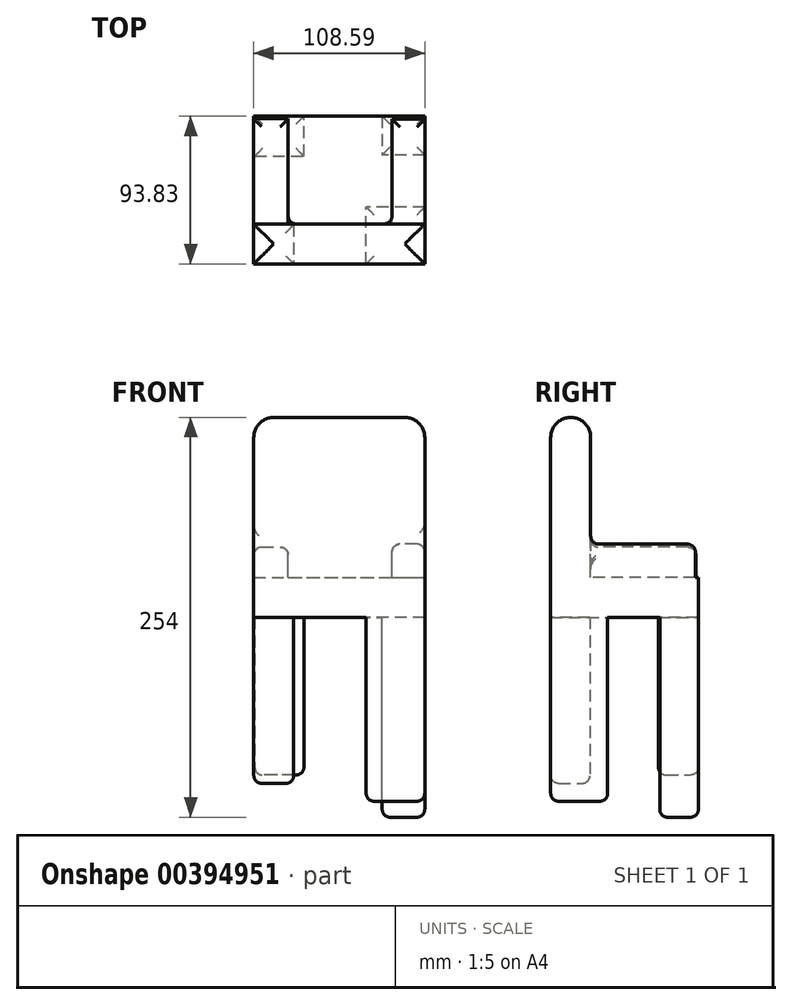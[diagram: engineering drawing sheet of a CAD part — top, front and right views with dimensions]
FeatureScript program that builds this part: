
annotation { "Feature Type Name" : "Feature", "Feature Type Description" : "" }
export const myFeature = defineFeature(function(context is Context, id is Id, definition is map)
    precondition{}
    {
        {
            var Q0;
            Q0=qCreatedBy(makeId("Top.planeOp"),FACE);
            var sketch = newSketch(context, id + "F0", { "sketchPlane" : qUnion([Q0])});
            skLineSegment(sketch, "E0.bottom", {"start": v(-122.47, 127.56) * mm, "end": v(-13.88, 127.56) * mm});
            skLineSegment(sketch, "E0.top", {"start": v(-122.47, 33.73) * mm, "end": v(-13.88, 33.73) * mm});
            skLineSegment(sketch, "E0.left", {"start": v(-122.47, 127.56) * mm, "end": v(-122.47, 33.73) * mm});
            skLineSegment(sketch, "E0.right", {"start": v(-13.88, 127.56) * mm, "end": v(-13.88, 33.73) * mm});
            skSolve(sketch);
        }
        {
            var Q0;
            Q0 = qSketchRegion(id + "F0", true);
            extrude(context, id + "F1", {"entities" : qUnion([Q0]), "depth" : 25.4 * mm});
        }
        {
            var Q0;
            Q0=makeQuery(id+"F1.opExtrude","CAP_FACE",FACE,{"disambiguationData":[OSD([sQuery(id+"F0.wireOp",EDGE,"E0.bottom"),sQuery(id+"F0.wireOp",EDGE,"E0.top"),sQuery(id+"F0.wireOp",EDGE,"E0.left"),sQuery(id+"F0.wireOp",EDGE,"E0.right")])],"isStart":false});
            var sketch = newSketch(context, id + "F2", { "sketchPlane" : qUnion([Q0])});
            skLineSegment(sketch, "E1.bottom", {"start": v(-122.47, 33.73) * mm, "end": v(-13.88, 33.73) * mm});
            skLineSegment(sketch, "E1.top", {"start": v(-122.47, 59.13) * mm, "end": v(-13.88, 59.13) * mm});
            skLineSegment(sketch, "E1.left", {"start": v(-122.47, 33.73) * mm, "end": v(-122.47, 59.13) * mm});
            skLineSegment(sketch, "E1.right", {"start": v(-13.88, 33.73) * mm, "end": v(-13.88, 59.13) * mm});
            skSolve(sketch);
        }
        {
            var Q0;
            Q0 = qSketchRegion(id + "F2", true);
            extrude(context, id + "F3", {"entities" : qUnion([Q0]), "operationType" : NewBodyOperationType.ADD, "depth" : 101.6 * mm});
        }
        {
            var Q0;
            Q0=makeQuery(id+"F1.opExtrude","SWEPT_FACE",FACE,{"disambiguationData":[OSD([sQuery(id+"F0.wireOp",EDGE,"E0.bottom")])]});
            var sketch = newSketch(context, id + "F4", { "sketchPlane" : qUnion([Q0])});
            skLineSegment(sketch, "E2.bottom", {"start": v(90.66, 0) * mm, "end": v(121.85, 0) * mm});
            skLineSegment(sketch, "E2.top", {"start": v(90.66, -100.2) * mm, "end": v(121.85, -100.2) * mm});
            skLineSegment(sketch, "E2.left", {"start": v(90.66, 0) * mm, "end": v(90.66, -100.2) * mm});
            skLineSegment(sketch, "E2.right", {"start": v(121.85, 0) * mm, "end": v(121.85, -100.2) * mm});
            skSolve(sketch);
        }
        {
            var Q0;
            Q0 = qSketchRegion(id + "F4", true);
            extrude(context, id + "F5", {"entities" : qUnion([Q0]), "operationType" : NewBodyOperationType.ADD, "oppositeDirection" : true, "depth" : 25.4 * mm});
        }
        {
            var Q0;
            Q0=makeQuery(id+"F3.boolean.opBoolean","MERGE",FACE,{"derivedFrom":[makeQuery(id+"F1.opExtrude","SWEPT_FACE",FACE,{"disambiguationData":[OSD([sQuery(id+"F0.wireOp",EDGE,"E0.left")])]}),makeQuery(id+"F3.opExtrude","SWEPT_FACE",FACE,{"disambiguationData":[OSD([sQuery(id+"F2.wireOp",EDGE,"E1.left")])]})]});
            var sketch = newSketch(context, id + "F6", { "sketchPlane" : qUnion([Q0])});
            skLineSegment(sketch, "E3.bottom", {"start": v(-33.73, 0) * mm, "end": v(-58.71, 0) * mm});
            skLineSegment(sketch, "E3.top", {"start": v(-33.73, -105.42) * mm, "end": v(-58.71, -105.42) * mm});
            skLineSegment(sketch, "E3.left", {"start": v(-33.73, 0) * mm, "end": v(-33.73, -105.42) * mm});
            skLineSegment(sketch, "E3.right", {"start": v(-58.71, 0) * mm, "end": v(-58.71, -105.42) * mm});
            skSolve(sketch);
        }
        {
            var Q0;
            Q0 = qSketchRegion(id + "F6", true);
            extrude(context, id + "F7", {"entities" : qUnion([Q0]), "oppositeDirection" : true, "depth" : 25.4 * mm});
        }
        {
            var Q0;
            Q0=makeQuery(id+"F1.opExtrude","CAP_FACE",FACE,{"disambiguationData":[OSD([sQuery(id+"F0.wireOp",EDGE,"E0.bottom"),sQuery(id+"F0.wireOp",EDGE,"E0.top"),sQuery(id+"F0.wireOp",EDGE,"E0.left"),sQuery(id+"F0.wireOp",EDGE,"E0.right")])],"isStart":true});
            var sketch = newSketch(context, id + "F8", { "sketchPlane" : qUnion([Q0])});
            skLineSegment(sketch, "E4.bottom", {"start": v(-13.88, -33.73) * mm, "end": v(-51.1, -33.73) * mm});
            skLineSegment(sketch, "E4.top", {"start": v(-13.88, -69.92) * mm, "end": v(-51.1, -69.92) * mm});
            skLineSegment(sketch, "E4.left", {"start": v(-13.88, -33.73) * mm, "end": v(-13.88, -69.92) * mm});
            skLineSegment(sketch, "E4.right", {"start": v(-51.1, -33.73) * mm, "end": v(-51.1, -69.92) * mm});
            skSolve(sketch);
        }
        {
            var Q0;
            Q0 = qSketchRegion(id + "F8", true);
            extrude(context, id + "F9", {"entities" : qUnion([Q0]), "operationType" : NewBodyOperationType.ADD, "depth" : 116.84 * mm});
        }
        {
            var Q0;
            Q0=makeQuery(id+"F1.opExtrude","CAP_FACE",FACE,{"disambiguationData":[OSD([sQuery(id+"F0.wireOp",EDGE,"E0.bottom"),sQuery(id+"F0.wireOp",EDGE,"E0.top"),sQuery(id+"F0.wireOp",EDGE,"E0.left"),sQuery(id+"F0.wireOp",EDGE,"E0.right")])],"isStart":true});
            var sketch = newSketch(context, id + "F10", { "sketchPlane" : qUnion([Q0])});
            skLineSegment(sketch, "E5.bottom", {"start": v(-13.88, -127.56) * mm, "end": v(-40.9, -127.56) * mm});
            skLineSegment(sketch, "E5.top", {"start": v(-13.88, -102.99) * mm, "end": v(-40.9, -102.99) * mm});
            skLineSegment(sketch, "E5.left", {"start": v(-13.88, -127.56) * mm, "end": v(-13.88, -102.99) * mm});
            skLineSegment(sketch, "E5.right", {"start": v(-40.9, -127.56) * mm, "end": v(-40.9, -102.99) * mm});
            skSolve(sketch);
        }
        {
            var Q0;
            Q0 = qSketchRegion(id + "F10", true);
            extrude(context, id + "F11", {"entities" : qUnion([Q0]), "operationType" : NewBodyOperationType.ADD, "depth" : 127 * mm});
        }
        {
            var Q0;
            Q0=makeQuery(id+"F3.opExtrude","SWEPT_FACE",FACE,{"disambiguationData":[OSD([sQuery(id+"F2.wireOp",EDGE,"E1.top")])]});
            var sketch = newSketch(context, id + "F12", { "sketchPlane" : qUnion([Q0])});
            skLineSegment(sketch, "E6.bottom", {"start": v(13.88, 25.4) * mm, "end": v(34.72, 25.4) * mm});
            skLineSegment(sketch, "E6.top", {"start": v(13.88, 46.54) * mm, "end": v(34.72, 46.54) * mm});
            skLineSegment(sketch, "E6.left", {"start": v(13.88, 25.4) * mm, "end": v(13.88, 46.54) * mm});
            skLineSegment(sketch, "E6.right", {"start": v(34.72, 25.4) * mm, "end": v(34.72, 46.54) * mm});
            skSolve(sketch);
        }
        {
            var Q0;
            Q0 = qSketchRegion(id + "F12", true);
            extrude(context, id + "F13", {"entities" : qUnion([Q0]), "operationType" : NewBodyOperationType.ADD, "depth" : 66.55 * mm});
        }
        {
            var Q0;
            Q0=makeQuery(id+"F3.opExtrude","SWEPT_FACE",FACE,{"disambiguationData":[OSD([sQuery(id+"F2.wireOp",EDGE,"E1.top")])]});
            var sketch = newSketch(context, id + "F14", { "sketchPlane" : qUnion([Q0])});
            skLineSegment(sketch, "E7.bottom", {"start": v(122.47, 25.4) * mm, "end": v(100.58, 25.4) * mm});
            skLineSegment(sketch, "E7.top", {"start": v(122.47, 44.57) * mm, "end": v(100.58, 44.57) * mm});
            skLineSegment(sketch, "E7.left", {"start": v(122.47, 25.4) * mm, "end": v(122.47, 44.57) * mm});
            skLineSegment(sketch, "E7.right", {"start": v(100.58, 25.4) * mm, "end": v(100.58, 44.57) * mm});
            skSolve(sketch);
        }
        {
            var Q0;
            Q0 = qSketchRegion(id + "F14", true);
            extrude(context, id + "F15", {"entities" : qUnion([Q0]), "operationType" : NewBodyOperationType.ADD, "depth" : 66.8 * mm});
        }
        {
            var Q0;
            Q0=makeQuery(id+"F13.opExtrude","SWEPT_FACE",FACE,{"disambiguationData":[OSD([sQuery(id+"F12.wireOp",EDGE,"E6.top")])]});
            fillet(context, id + "F16", {"entities" : qUnion([Q0]), "radius" : 5.08 * mm, "tangentPropagation" : true, "allowEdgeOverflow" : false});
        }
        {
            var Q0;
            Q0=makeQuery(id+"F15.opExtrude","SWEPT_FACE",FACE,{"disambiguationData":[OSD([sQuery(id+"F14.wireOp",EDGE,"E7.top")])]});
            fillet(context, id + "F17", {"entities" : qUnion([Q0]), "radius" : 5.08 * mm, "tangentPropagation" : true, "allowEdgeOverflow" : false});
        }
        {
            var Q0;
            Q0=makeQuery(id+"F3.opExtrude","CAP_FACE",FACE,{"disambiguationData":[OSD([sQuery(id+"F2.wireOp",EDGE,"E1.bottom"),sQuery(id+"F2.wireOp",EDGE,"E1.top"),sQuery(id+"F2.wireOp",EDGE,"E1.left"),sQuery(id+"F2.wireOp",EDGE,"E1.right")])],"isStart":false});
            fillet(context, id + "F18", {"entities" : qUnion([Q0]), "radius" : 12.7 * mm, "tangentPropagation" : true, "allowEdgeOverflow" : false});
        }
        {
            var Q0;
            Q0=makeQuery(id+"F9.opExtrude","CAP_FACE",FACE,{"disambiguationData":[OSD([sQuery(id+"F8.wireOp",EDGE,"E4.bottom"),sQuery(id+"F8.wireOp",EDGE,"E4.top"),sQuery(id+"F8.wireOp",EDGE,"E4.left"),sQuery(id+"F8.wireOp",EDGE,"E4.right")])],"isStart":false});
            fillet(context, id + "F19", {"entities" : qUnion([Q0]), "radius" : 5.08 * mm, "tangentPropagation" : true, "allowEdgeOverflow" : false});
        }
        {
            var Q0;
            Q0=makeQuery(id+"F11.opExtrude","CAP_FACE",FACE,{"disambiguationData":[OSD([sQuery(id+"F10.wireOp",EDGE,"E5.bottom"),sQuery(id+"F10.wireOp",EDGE,"E5.top"),sQuery(id+"F10.wireOp",EDGE,"E5.left"),sQuery(id+"F10.wireOp",EDGE,"E5.right")])],"isStart":false});
            fillet(context, id + "F20", {"entities" : qUnion([Q0]), "radius" : 5.08 * mm, "tangentPropagation" : true, "allowEdgeOverflow" : false});
        }
        {
            var Q0;
            Q0=makeQuery(id+"F5.opExtrude","SWEPT_FACE",FACE,{"disambiguationData":[OSD([sQuery(id+"F4.wireOp",EDGE,"E2.top")])]});
            fillet(context, id + "F21", {"entities" : qUnion([Q0]), "radius" : 5.08 * mm, "tangentPropagation" : true, "allowEdgeOverflow" : false});
        }
        {
            var Q0;
            Q0=makeQuery(id+"F7.opExtrude","SWEPT_FACE",FACE,{"disambiguationData":[OSD([sQuery(id+"F6.wireOp",EDGE,"E3.top")])]});
            fillet(context, id + "F22", {"entities" : qUnion([Q0]), "radius" : 5.08 * mm, "tangentPropagation" : true, "allowEdgeOverflow" : false});
        }
    });
